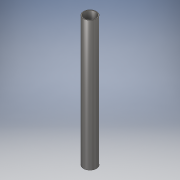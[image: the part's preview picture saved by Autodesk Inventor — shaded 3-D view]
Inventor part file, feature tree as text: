
AUTODESK INVENTOR PART (.ipt)
format: ipt  version: 2018 (Build 220112000, 112)  size: 99,328 bytes
history: native  units: in
note: dims shown in document units (in); Inventor stores cm internally (conversion verified against a paired STEP export)
features: extrude x1, sketch x1
ambient origin geometry x8: Origin, YZ Plane, XZ Plane, XY Plane, X Axis, Y Axis, Z Axis, Center Point
bodies: Solid1 (feature_tree)
feature tree (2):
  extrude  "Extrusion1"  Depth=5.0in
  sketch  "Sketch1"  dims[d0=0.5in d1=0.03in d2=5.0in d3=0.0in]
